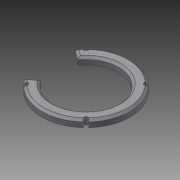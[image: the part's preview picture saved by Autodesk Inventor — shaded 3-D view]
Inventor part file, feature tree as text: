
AUTODESK INVENTOR PART (.ipt)
format: ipt  version: 2018 (Build 220112000, 112)  size: 135,168 bytes
history: native  units: mm
features: other x4, reference x4, extrude x2, sketch x2, chamfer x1
ambient origin geometry x8: Origin, YZ Plane, XZ Plane, XY Plane, X Axis, Y Axis, Z Axis, Center Point
bodies: Body1 (feature_tree)
feature tree (13):
  other  "ソリッド1"
  extrude  "押し出し1"  Depth=23.0mm
  chamfer  "面取り1"  Distance=8.0mm
  extrude  "押し出し2"  Depth=50.614548mm
  sketch  "スケッチ1"
  sketch  "スケッチ2"
  reference  "参照1"
  reference  "参照2"
  reference  "参照3"
  reference  "参照4"
  parser-record x1  (decoder bookkeeping rows leaked as tree rows — omitted from the tree; the rows remain in map.json)
  other  "topassy.iam"
  other  "topcover:1"
note: 1 file-system path scrubbed to <path> (originals preserved in map.json)
